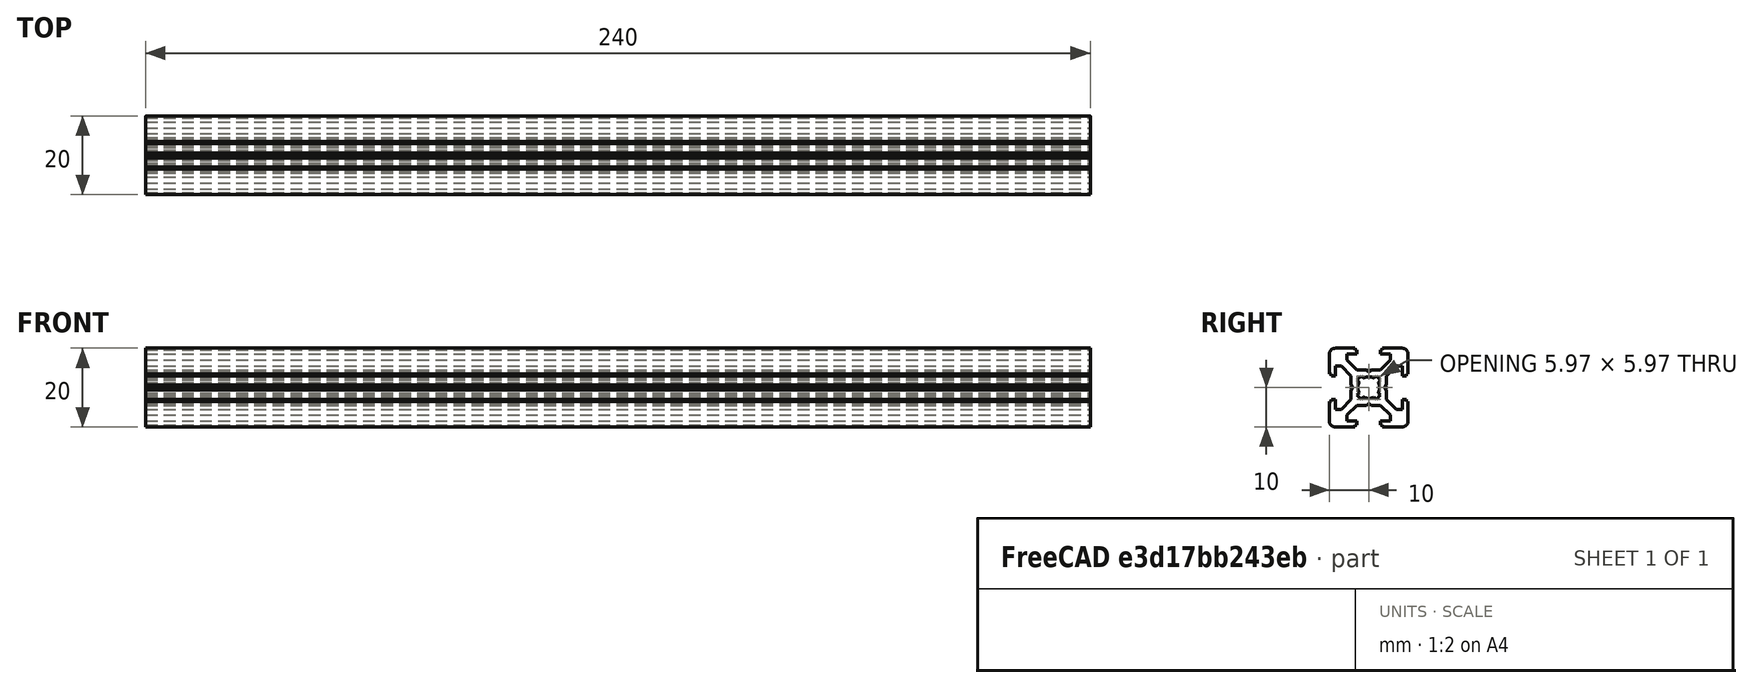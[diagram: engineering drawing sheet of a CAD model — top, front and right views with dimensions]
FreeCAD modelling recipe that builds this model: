
FCSTD DOCUMENT  (FreeCAD 0.19R)
Label: Tslot24
License: All rights reserved
LicenseURL: http://en.wikipedia.org/wiki/All_rights_reserved
objects: Sketcher::SketchObject×1, PartDesign::Pad×1, PartDesign::Body×1
note: 4 computed .brp shape members not serialized (recipe doc carries the construction recipe); baked Part::Feature solids carry a one-line shape summary decoded from their .brp

FEATURE [Sketcher::SketchObject] Sketch  label="T-Slot-Skizze"
  FullyConstrained = true
  MapMode = 5
  Placement = pos=(0,0,0) rot=(0.57735,0.57735,0.57735;2.0944rad)
  Support = -> [YZ_Plane]
  sketch-geometry (98):
    g0: LineSegment StartX=0 StartY=4.1 StartZ=0 EndX=0.65 EndY=4.5 EndZ=0
    g1: LineSegment StartX=0.65 StartY=4.5 StartZ=0 EndX=3 EndY=4.5 EndZ=0
    g2: LineSegment StartX=3 StartY=4.5 StartZ=0 EndX=5.5 EndY=7 EndZ=0
    g3: LineSegment StartX=5.5 StartY=7 StartZ=0 EndX=5.5 EndY=8.5 EndZ=0
    g4: LineSegment StartX=5.5 StartY=8.5 StartZ=0 EndX=3 EndY=8.5 EndZ=0
    g5: LineSegment StartX=3 StartY=8.5 StartZ=0 EndX=3 EndY=9.5 EndZ=0
    g6: LineSegment StartX=3 StartY=9.5 StartZ=0 EndX=3.5 EndY=9.5 EndZ=0
    g7: LineSegment StartX=3.5 StartY=9.5 StartZ=0 EndX=3.5 EndY=10 EndZ=0
    g8: LineSegment StartX=3.5 StartY=10 StartZ=0 EndX=8.5 EndY=10 EndZ=0
    g9: LineSegment StartX=10 StartY=8.5 StartZ=0 EndX=10 EndY=3.5 EndZ=0
    g10: LineSegment StartX=10 StartY=3.5 StartZ=0 EndX=9.5 EndY=3.5 EndZ=0
    g11: LineSegment StartX=9.5 StartY=3.5 StartZ=0 EndX=9.5 EndY=3 EndZ=0
    g12: LineSegment StartX=9.5 StartY=3 StartZ=0 EndX=8.5 EndY=3 EndZ=0
    g13: LineSegment StartX=8.5 StartY=3 StartZ=0 EndX=8.5 EndY=5.5 EndZ=0
    g14: LineSegment StartX=8.5 StartY=5.5 StartZ=0 EndX=7 EndY=5.5 EndZ=0
    g15: LineSegment StartX=7 StartY=5.5 StartZ=0 EndX=4.5 EndY=3 EndZ=0
    g16: LineSegment StartX=4.5 StartY=3 StartZ=0 EndX=4.5 EndY=0.65 EndZ=0
    g17: LineSegment StartX=4.5 StartY=0.65 StartZ=0 EndX=4.1 EndY=0 EndZ=0
    g18: ArcOfCircle CenterX=8.5 CenterY=8.5 CenterZ=0 NormalX=0 NormalY=0 NormalZ=1 AngleXU=0 Radius=1.5 StartAngle=0 EndAngle=1.5708
    g19: LineSegment StartX=0 StartY=-4.1 StartZ=0 EndX=0.65 EndY=-4.5 EndZ=0
    g20: LineSegment StartX=0.65 StartY=-4.5 StartZ=0 EndX=3 EndY=-4.5 EndZ=0
    g21: LineSegment StartX=3 StartY=-4.5 StartZ=0 EndX=5.5 EndY=-7 EndZ=0
    g22: LineSegment StartX=5.5 StartY=-7 StartZ=0 EndX=5.5 EndY=-8.5 EndZ=0
    g23: LineSegment StartX=5.5 StartY=-8.5 StartZ=0 EndX=3 EndY=-8.5 EndZ=0
    g24: LineSegment StartX=3 StartY=-8.5 StartZ=0 EndX=3 EndY=-9.5 EndZ=0
    g25: LineSegment StartX=3 StartY=-9.5 StartZ=0 EndX=3.5 EndY=-9.5 EndZ=0
    g26: LineSegment StartX=3.5 StartY=-9.5 StartZ=0 EndX=3.5 EndY=-10 EndZ=0
    g27: LineSegment StartX=3.5 StartY=-10 StartZ=0 EndX=8.5 EndY=-10 EndZ=0
    g28: LineSegment StartX=10 StartY=-8.5 StartZ=0 EndX=10 EndY=-3.5 EndZ=0
    g29: LineSegment StartX=10 StartY=-3.5 StartZ=0 EndX=9.5 EndY=-3.5 EndZ=0
    g30: LineSegment StartX=9.5 StartY=-3.5 StartZ=0 EndX=9.5 EndY=-3 EndZ=0
    g31: LineSegment StartX=9.5 StartY=-3 StartZ=0 EndX=8.5 EndY=-3 EndZ=0
    g32: LineSegment StartX=8.5 StartY=-3 StartZ=0 EndX=8.5 EndY=-5.5 EndZ=0
    g33: LineSegment StartX=8.5 StartY=-5.5 StartZ=0 EndX=7 EndY=-5.5 EndZ=0
    g34: LineSegment StartX=7 StartY=-5.5 StartZ=0 EndX=4.5 EndY=-3 EndZ=0
    g35: LineSegment StartX=4.5 StartY=-3 StartZ=0 EndX=4.5 EndY=-0.65 EndZ=0
    g36: ArcOfCircle CenterX=8.5 CenterY=-8.5 CenterZ=0 NormalX=0 NormalY=0 NormalZ=1 AngleXU=0 Radius=1.5 StartAngle=4.71239 EndAngle=6.28319
    g37: LineSegment StartX=4.5 StartY=-0.65 StartZ=0 EndX=4.1 EndY=0 EndZ=0
    g38: LineSegment StartX=0 StartY=-4.1 StartZ=0 EndX=-0.65 EndY=-4.5 EndZ=0
    g39: LineSegment StartX=-0.65 StartY=-4.5 StartZ=0 EndX=-3 EndY=-4.5 EndZ=0
    g40: LineSegment StartX=-3 StartY=-4.5 StartZ=0 EndX=-5.5 EndY=-7 EndZ=0
    g41: LineSegment StartX=-5.5 StartY=-7 StartZ=0 EndX=-5.5 EndY=-8.5 EndZ=0
    g42: LineSegment StartX=-5.5 StartY=-8.5 StartZ=0 EndX=-3 EndY=-8.5 EndZ=0
    g43: LineSegment StartX=-3 StartY=-8.5 StartZ=0 EndX=-3 EndY=-9.5 EndZ=0
    g44: LineSegment StartX=-3 StartY=-9.5 StartZ=0 EndX=-3.5 EndY=-9.5 EndZ=0
    g45: LineSegment StartX=-3.5 StartY=-9.5 StartZ=0 EndX=-3.5 EndY=-10 EndZ=0
    g46: LineSegment StartX=-3.5 StartY=-10 StartZ=0 EndX=-8.5 EndY=-10 EndZ=0
    g47: LineSegment StartX=-10 StartY=-8.5 StartZ=0 EndX=-10 EndY=-3.5 EndZ=0
    g48: LineSegment StartX=-10 StartY=-3.5 StartZ=0 EndX=-9.5 EndY=-3.5 EndZ=0
    g49: LineSegment StartX=-9.5 StartY=-3.5 StartZ=0 EndX=-9.5 EndY=-3 EndZ=0
    g50: LineSegment StartX=-9.5 StartY=-3 StartZ=0 EndX=-8.5 EndY=-3 EndZ=0
    g51: LineSegment StartX=-8.5 StartY=-3 StartZ=0 EndX=-8.5 EndY=-5.5 EndZ=0
    g52: LineSegment StartX=-8.5 StartY=-5.5 StartZ=0 EndX=-7 EndY=-5.5 EndZ=0
    g53: LineSegment StartX=-7 StartY=-5.5 StartZ=0 EndX=-4.5 EndY=-3 EndZ=0
    g54: LineSegment StartX=-4.5 StartY=-3 StartZ=0 EndX=-4.5 EndY=-0.65 EndZ=0
    g55: ArcOfCircle CenterX=-8.5 CenterY=-8.5 CenterZ=0 NormalX=0 NormalY=0 NormalZ=1 AngleXU=0 Radius=1.5 StartAngle=3.14159 EndAngle=4.71239
    g56: LineSegment StartX=-4.5 StartY=-0.65 StartZ=0 EndX=-4.1 EndY=0 EndZ=0
    g57: LineSegment StartX=-0.65 StartY=4.5 StartZ=0 EndX=-3 EndY=4.5 EndZ=0
    g58: LineSegment StartX=-3 StartY=4.5 StartZ=0 EndX=-5.5 EndY=7 EndZ=0
    g59: LineSegment StartX=-5.5 StartY=7 StartZ=0 EndX=-5.5 EndY=8.5 EndZ=0
    g60: LineSegment StartX=-5.5 StartY=8.5 StartZ=0 EndX=-3 EndY=8.5 EndZ=0
    g61: LineSegment StartX=-3 StartY=8.5 StartZ=0 EndX=-3 EndY=9.5 EndZ=0
    g62: LineSegment StartX=-3 StartY=9.5 StartZ=0 EndX=-3.5 EndY=9.5 EndZ=0
    g63: LineSegment StartX=-3.5 StartY=9.5 StartZ=0 EndX=-3.5 EndY=10 EndZ=0
    g64: LineSegment StartX=-3.5 StartY=10 StartZ=0 EndX=-8.5 EndY=10 EndZ=0
    g65: LineSegment StartX=-10 StartY=8.5 StartZ=0 EndX=-10 EndY=3.5 EndZ=0
    g66: LineSegment StartX=-10 StartY=3.5 StartZ=0 EndX=-9.5 EndY=3.5 EndZ=0
    g67: LineSegment StartX=-9.5 StartY=3.5 StartZ=0 EndX=-9.5 EndY=3 EndZ=0
    g68: LineSegment StartX=-9.5 StartY=3 StartZ=0 EndX=-8.5 EndY=3 EndZ=0
    g69: LineSegment StartX=-8.5 StartY=3 StartZ=0 EndX=-8.5 EndY=5.5 EndZ=0
    g70: LineSegment StartX=-8.5 StartY=5.5 StartZ=0 EndX=-7 EndY=5.5 EndZ=0
    g71: LineSegment StartX=-7 StartY=5.5 StartZ=0 EndX=-4.5 EndY=3 EndZ=0
    g72: LineSegment StartX=-4.5 StartY=3 StartZ=0 EndX=-4.5 EndY=0.65 EndZ=0
    g73: ArcOfCircle CenterX=-8.5 CenterY=8.5 CenterZ=0 NormalX=0 NormalY=0 NormalZ=1 AngleXU=0 Radius=1.5 StartAngle=1.5708 EndAngle=3.14159
    g74: LineSegment StartX=-4.5 StartY=0.65 StartZ=0 EndX=-4.1 EndY=0 EndZ=0
    g75: LineSegment StartX=0 StartY=4.1 StartZ=0 EndX=-0.65 EndY=4.5 EndZ=0
    g76: Circle CenterX=0 CenterY=0 CenterZ=0 NormalX=0 NormalY=0 NormalZ=1 AngleXU=0 Radius=3.55
    g77: Circle CenterX=0 CenterY=0 CenterZ=0 NormalX=0 NormalY=0 NormalZ=1 AngleXU=0 Radius=2.75
    g78: LineSegment StartX=1.3405 StartY=2.40116 StartZ=0 EndX=1.92324 EndY=2.9839 EndZ=0
    g79: LineSegment StartX=1.92324 StartY=2.9839 StartZ=0 EndX=2.9839 EndY=1.92324 EndZ=0
    g80: LineSegment StartX=2.9839 StartY=1.92324 StartZ=0 EndX=2.40116 EndY=1.3405 EndZ=0
    g81: ArcOfCircle CenterX=0 CenterY=0 CenterZ=0 NormalX=0 NormalY=0 NormalZ=1 AngleXU=0 Radius=2.75 StartAngle=0 EndAngle=0.509172
    g82: ArcOfCircle CenterX=0 CenterY=0 CenterZ=0 NormalX=0 NormalY=0 NormalZ=1 AngleXU=0 Radius=2.75 StartAngle=1.06162 EndAngle=1.5708
    g83: LineSegment StartX=-1.3405 StartY=2.40116 StartZ=0 EndX=-1.92324 EndY=2.9839 EndZ=0
    g84: LineSegment StartX=-1.92324 StartY=2.9839 StartZ=0 EndX=-2.9839 EndY=1.92324 EndZ=0
    g85: LineSegment StartX=-2.9839 StartY=1.92324 StartZ=0 EndX=-2.40116 EndY=1.3405 EndZ=0
    g86: ArcOfCircle CenterX=-1.3e-15 CenterY=6e-16 CenterZ=0 NormalX=0 NormalY=0 NormalZ=1 AngleXU=0 Radius=2.75 StartAngle=2.63242 EndAngle=3.14159
    g87: ArcOfCircle CenterX=-1.3e-15 CenterY=6e-16 CenterZ=0 NormalX=0 NormalY=0 NormalZ=1 AngleXU=0 Radius=2.75 StartAngle=1.5708 EndAngle=2.07997
    g88: LineSegment StartX=-1.34051 StartY=-2.40115 StartZ=0 EndX=-1.92325 EndY=-2.98389 EndZ=0
    g89: LineSegment StartX=-1.92325 StartY=-2.98389 StartZ=0 EndX=-2.9839 EndY=-1.92323 EndZ=0
    g90: LineSegment StartX=-2.9839 StartY=-1.92323 StartZ=0 EndX=-2.40116 EndY=-1.34049 EndZ=0
    g91: ArcOfCircle CenterX=-3e-16 CenterY=2e-16 CenterZ=0 NormalX=0 NormalY=0 NormalZ=1 AngleXU=0 Radius=2.75 StartAngle=3.14159 EndAngle=3.65076
    g92: ArcOfCircle CenterX=-3e-16 CenterY=2e-16 CenterZ=0 NormalX=0 NormalY=0 NormalZ=1 AngleXU=0 Radius=2.75 StartAngle=4.20321 EndAngle=4.71239
    g93: LineSegment StartX=1.34051 StartY=-2.40115 StartZ=0 EndX=1.92325 EndY=-2.98389 EndZ=0
    g94: LineSegment StartX=1.92325 StartY=-2.98389 StartZ=0 EndX=2.9839 EndY=-1.92323 EndZ=0
    g95: LineSegment StartX=2.9839 StartY=-1.92323 StartZ=0 EndX=2.40116 EndY=-1.34049 EndZ=0
    g96: ArcOfCircle CenterX=3e-16 CenterY=2e-16 CenterZ=0 NormalX=0 NormalY=0 NormalZ=1 AngleXU=0 Radius=2.75 StartAngle=4.71239 EndAngle=5.22156
    g97: ArcOfCircle CenterX=3e-16 CenterY=2e-16 CenterZ=0 NormalX=0 NormalY=0 NormalZ=1 AngleXU=0 Radius=2.75 StartAngle=5.77402 EndAngle=6.28319
  constraints (291):
    c: PointOnObject(g0,g-2)
    c: Coincident(g0,g1)
    c: Horizontal(g1)
    c: Coincident(g1,g2)
    c: Coincident(g2,g3)
    c: Vertical(g3)
    c: Coincident(g3,g4)
    c: Horizontal(g4)
    c: Coincident(g4,g5)
    c: Vertical(g5)
    c: Coincident(g5,g6)
    c: Horizontal(g6)
    c: Coincident(g6,g7)
    c: Coincident(g7,g8)
    c: Horizontal(g8)
    c: Vertical(g7)
    c: DistanceX(g-1,g5) = 3
    c: DistanceY(g4,g7) = 1.5
    c: DistanceY(g0,g7) = 5.5
    c: DistanceY(g3,g3) = 1.5
    c: DistanceY(g4,g5) = 1
    c: DistanceX(g-1,g1) = 3
    c: DistanceX(g-1,g7) = 3.5
    c: DistanceX(g0,g0) = 0.65
    c: DistanceY(g0,g0) = 0.4
    c: DistanceX(g-1,g3) = 5.5
    c: Vertical(g9)
    c: Coincident(g9,g10)
    c: Coincident(g10,g11)
    c: Coincident(g11,g12)
    c: Coincident(g12,g13)
    c: Vertical(g13)
    c: Coincident(g13,g14)
    c: Horizontal(g14)
    c: Coincident(g14,g15)
    c: Coincident(g15,g16)
    c: Vertical(g16)
    c: Coincident(g16,g17)
    c: PointOnObject(g17,g-1)
    c: Horizontal(g10)
    c: Horizontal(g12)
    c: Vertical(g11)
    c: Equal(g17,g0)
    c: Equal(g1,g16)
    c: Equal(g15,g2)
    c: Equal(g3,g14)
    c: Equal(g13,g4)
    c: Equal(g12,g5)
    c: Parallel(g15,g2)
    c: Equal(g11,g6)
    c: Equal(g10,g7)
    c: Equal(g9,g8)
    c: Tangent(g8,g18) = 1.5708
    c: Tangent(g9,g18) = 1.5708
    c: Radius(g18) = 1.5
    c: DistanceY(g-1,g8) = 10
    c: DistanceX(g-1,g9) = 10
    c: Coincident(g19,g20)
    c: Horizontal(g20)
    c: Coincident(g20,g21)
    c: Coincident(g21,g22)
    c: Vertical(g22)
    c: Coincident(g22,g23)
    c: Horizontal(g23)
    c: Coincident(g23,g24)
    c: Vertical(g24)
    c: Coincident(g24,g25)
    c: Horizontal(g25)
    c: Coincident(g25,g26)
    c: Coincident(g26,g27)
    c: Horizontal(g27)
    c: Vertical(g26)
    c: Vertical(g28)
    c: Coincident(g28,g29)
    c: Coincident(g29,g30)
    c: Coincident(g30,g31)
    c: Coincident(g31,g32)
    c: Vertical(g32)
    c: Coincident(g32,g33)
    c: Horizontal(g33)
    c: Coincident(g33,g34)
    c: Coincident(g34,g35)
    c: Vertical(g35)
    c: Coincident(g35,g37)
    c: Horizontal(g29)
    c: Horizontal(g31)
    c: Vertical(g30)
    c: Equal(g37,g19)
    c: Equal(g20,g35)
    c: Equal(g34,g21)
    c: Equal(g22,g33)
    c: Equal(g32,g23)
    c: Equal(g31,g24)
    c: Parallel(g34,g21)
    c: Equal(g30,g25)
    c: Equal(g29,g26)
    c: Equal(g28,g27)
    c: Tangent(g27,g36) = -1.5708
    c: Tangent(g28,g36) = -1.5708
    c: Radius(g36) = 1.5
    c: Equal(g9,g28)
    c: Equal(g12,g31)
    c: DistanceX(g-1,g28) = 10
    c: DistanceY(g27,g-1) = 10
    c: DistanceY(g30,g-1) = 3
    c: Equal(g33,g14)
    c: Equal(g35,g16)
    c: Equal(g17,g37)
    c: Coincident(g37,g17)
    c: Equal(g15,g34)
    c: PointOnObject(g19,g-2)
    c: DistanceY(g34,g-1) = 3
    c: DistanceX(g-1,g20) = 3
    c: Coincident(g38,g39)
    c: Horizontal(g39)
    c: Coincident(g39,g40)
    c: Coincident(g40,g41)
    c: Vertical(g41)
    c: Coincident(g41,g42)
    c: Horizontal(g42)
    c: Coincident(g42,g43)
    c: Vertical(g43)
    c: Coincident(g43,g44)
    c: Horizontal(g44)
    c: Coincident(g44,g45)
    c: Coincident(g45,g46)
    c: Horizontal(g46)
    c: Vertical(g45)
    c: Vertical(g47)
    c: Coincident(g47,g48)
    c: Coincident(g48,g49)
    c: Coincident(g49,g50)
    c: Coincident(g50,g51)
    c: Vertical(g51)
    c: Coincident(g51,g52)
    c: Horizontal(g52)
    c: Coincident(g52,g53)
    c: Coincident(g53,g54)
    c: Vertical(g54)
    c: Coincident(g54,g56)
    c: Horizontal(g48)
    c: Horizontal(g50)
    c: Vertical(g49)
    c: Equal(g39,g54)
    c: Equal(g53,g40)
    c: Equal(g41,g52)
    c: Equal(g51,g42)
    c: Equal(g50,g43)
    c: Parallel(g53,g40)
    c: Equal(g49,g44)
    c: Equal(g48,g45)
    c: Equal(g47,g46)
    c: Tangent(g46,g55) = 1.5708
    c: Tangent(g47,g55) = 1.5708
    c: Radius(g55) = 1.5
    c: Coincident(g38,g19)
    c: DistanceX(g39,g-1) = 3
    c: DistanceX(g38,g19) = 0.65
    c: DistanceY(g38,g19) = 0.4
    c: PointOnObject(g56,g-1)
    c: Equal(g56,g38)
    c: DistanceY(g53,g-1) = 3
    c: Equal(g22,g41)
    c: Equal(g42,g23)
    c: Equal(g24,g43)
    c: Equal(g25,g44)
    c: Equal(g26,g45)
    c: DistanceY(g46,g-1) = 10
    c: DistanceX(g47,g-1) = 10
    c: Coincident(g75,g57)
    c: Horizontal(g57)
    c: Coincident(g57,g58)
    c: Coincident(g58,g59)
    c: Vertical(g59)
    c: Coincident(g59,g60)
    c: Horizontal(g60)
    c: Coincident(g60,g61)
    c: Vertical(g61)
    c: Coincident(g61,g62)
    c: Horizontal(g62)
    c: Coincident(g62,g63)
    c: Coincident(g63,g64)
    c: Horizontal(g64)
    c: Vertical(g63)
    c: Vertical(g65)
    c: Coincident(g65,g66)
    c: Coincident(g66,g67)
    c: Coincident(g67,g68)
    c: Coincident(g68,g69)
    c: Vertical(g69)
    c: Coincident(g69,g70)
    c: Horizontal(g70)
    c: Coincident(g70,g71)
    c: Coincident(g71,g72)
    c: Vertical(g72)
    c: Coincident(g72,g74)
    c: Horizontal(g66)
    c: Horizontal(g68)
    c: Vertical(g67)
    c: Equal(g57,g72)
    c: Equal(g71,g58)
    c: Equal(g59,g70)
    c: Equal(g69,g60)
    c: Equal(g68,g61)
    c: Parallel(g71,g58)
    c: Equal(g67,g62)
    c: Equal(g66,g63)
    c: Equal(g65,g64)
    c: Tangent(g64,g73) = -1.5708
    c: Tangent(g65,g73) = -1.5708
    c: Radius(g73) = 1.5
    c: Equal(g74,g75)
    c: Coincident(g56,g74)
    c: Coincident(g0,g75)
    c: Equal(g0,g75)
    c: Equal(g1,g57)
    c: Equal(g2,g58)
    c: Equal(g3,g59)
    c: Equal(g4,g60)
    c: Equal(g5,g61)
    c: Equal(g6,g62)
    c: Equal(g7,g63)
    c: Equal(g8,g64)
    c: DistanceX(g65,g-1) = 10
    c: Coincident(g76,g-1)
    c: Coincident(g77,g-1)
    c: Radius(g76) = 3.55
    c: Radius(g77) = 2.75
    c: PointOnObject(g78,g77)
    c: PointOnObject(g78,g76)
    c: Coincident(g78,g79)
    c: PointOnObject(g79,g76)
    c: Coincident(g79,g80)
    c: PointOnObject(g80,g77)
    c: Coincident(g81,g-1)
    c: Coincident(g81,g80)
    c: Coincident(g82,g81)
    c: Coincident(g82,g78)
    c: Parallel(g78,g80)
    c: Parallel(g78,g2)
    c: Distance(g79) = 1.5
    c: Distance(g78,g80) = 1.5
    c: PointOnObject(g82,g-2)
    c: PointOnObject(g81,g-1)
    c: Coincident(g83,g84)
    c: Coincident(g84,g85)
    c: Coincident(g86,g85)
    c: Coincident(g87,g86)
    c: Coincident(g87,g83)
    c: Parallel(g83,g85)
    c: Distance(g84) = 1.5
    c: Distance(g83,g85) = 1.5
    c: Coincident(g82,g87)
    c: PointOnObject(g86,g-1)
    c: PointOnObject(g83,g76)
    c: PointOnObject(g83,g77)
    c: PointOnObject(g85,g77)
    c: PointOnObject(g84,g76)
    c: PointOnObject(g86,g77)
    c: Parallel(g85,g71)
    c: Coincident(g88,g89)
    c: Coincident(g89,g90)
    c: Coincident(g91,g90)
    c: Coincident(g92,g91)
    c: Coincident(g92,g88)
    c: Parallel(g88,g90)
    c: Distance(g89) = 1.5
    c: Distance(g88,g90) = 1.5
    c: PointOnObject(g88,g77)
    c: PointOnObject(g90,g77)
    c: Coincident(g86,g91)
    c: PointOnObject(g89,g76)
    c: PointOnObject(g88,g76)
    c: PointOnObject(g92,g-2)
    c: PointOnObject(g92,g77)
    c: Parallel(g88,g40)
    c: Coincident(g93,g94)
    c: Coincident(g94,g95)
    c: Coincident(g97,g95)
    c: Coincident(g96,g97)
    c: Coincident(g96,g93)
    c: Parallel(g93,g95)
    c: Distance(g94) = 1.5
    c: Distance(g93,g95) = 1.5
    c: Coincident(g81,g97)
    c: Coincident(g92,g96)
    c: PointOnObject(g93,g77)
    c: PointOnObject(g95,g77)
    c: PointOnObject(g94,g76)
    c: PointOnObject(g93,g76)
    c: Parallel(g93,g21)
FEATURE [PartDesign::Pad] Pad  label="T-Slot-Element"
  Direction = (1,1,1)
  Length = 240
  Length2 = 100
  Placement = pos=(0,0,0) rot=(0.57735,0.57735,0.57735;2.0944rad)
  Profile = -> Sketch
  Type = 0
FEATURE [PartDesign::Body] Body  label="T-Slot-Profil 20x20"
  Group = -> [Sketch,Pad]
  Origin = -> Origin
  Tip = -> Pad
